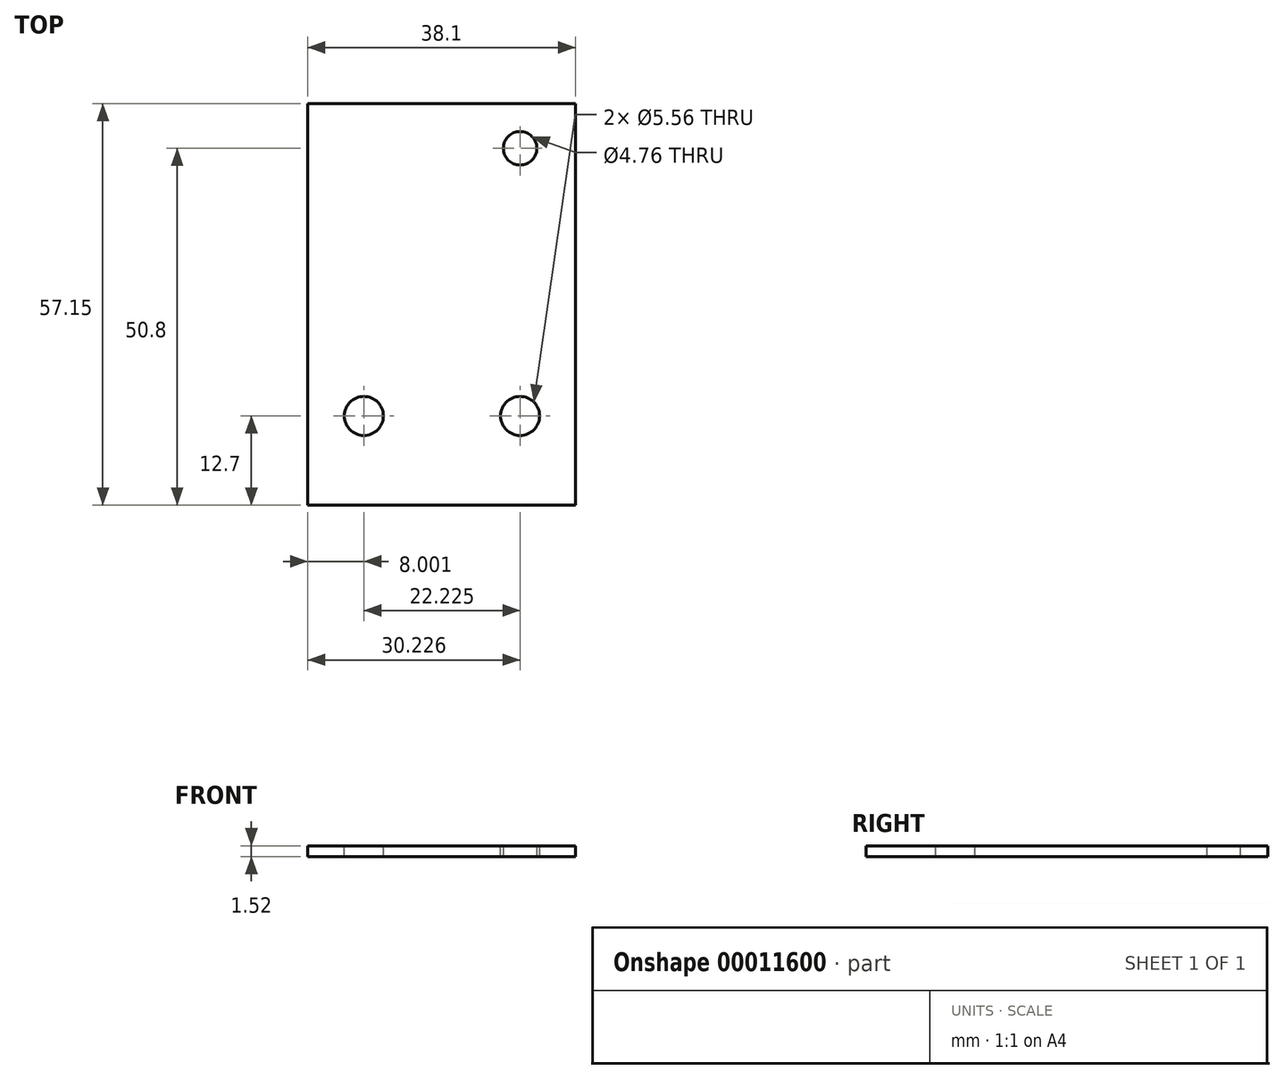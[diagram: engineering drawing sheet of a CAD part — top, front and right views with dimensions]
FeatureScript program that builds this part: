
annotation { "Feature Type Name" : "Feature", "Feature Type Description" : "" }
export const myFeature = defineFeature(function(context is Context, id is Id, definition is map)
    precondition{}
    {
        {
            var Q0;
            Q0=qCreatedBy(makeId("Top.planeOp"),FACE);
            var sketch = newSketch(context, id + "F0", { "sketchPlane" : qUnion([Q0])});
            skLineSegment(sketch, "E0.bottom", {"start": v(0, 0) * mm, "end": v(-38.1, 0) * mm});
            skLineSegment(sketch, "E0.top", {"start": v(0, -57.15) * mm, "end": v(-38.1, -57.15) * mm});
            skLineSegment(sketch, "E0.left", {"start": v(0, 0) * mm, "end": v(0, -57.15) * mm});
            skLineSegment(sketch, "E0.right", {"start": v(-38.1, 0) * mm, "end": v(-38.1, -57.15) * mm});
            skSolve(sketch);
        }
        {
            var Q0;
            Q0 = qSketchRegion(id + "F0", true);
            extrude(context, id + "F1", {"entities" : qUnion([Q0]), "depth" : 1.52 * mm});
        }
        {
            var Q0;
            Q0=qCreatedBy(makeId("Top.planeOp"),FACE);
            var sketch = newSketch(context, id + "F2", { "sketchPlane" : qUnion([Q0])});
            skPoint(sketch, "E1", {"position": v(-7.87, -6.35) * mm});
            skSolve(sketch);
        }
        {
            var Q0;
            Q0=makeQuery(id+"F1.opExtrude","CAP_FACE",FACE,{"disambiguationData":[OSD([sQuery(id+"F0.wireOp",EDGE,"E0.bottom"),sQuery(id+"F0.wireOp",EDGE,"E0.top"),sQuery(id+"F0.wireOp",EDGE,"E0.left"),sQuery(id+"F0.wireOp",EDGE,"E0.right")])],"isStart":false});
            var sketch = newSketch(context, id + "F3", { "sketchPlane" : qUnion([Q0])});
            skPoint(sketch, "E2", {"position": v(-7.87, -44.45) * mm});
            skPoint(sketch, "E3", {"position": v(-30.1, -44.45) * mm});
            skSolve(sketch);
        }
        {
            var Q0;
            Q0=sQuery(id+"F2.wireOp",VERTEX,"E1");
            var Q1;
            Q1=makeQuery(id+"F1.opExtrude","SWEPT_BODY",BODY,{"disambiguationData":[OSD([sQuery(id+"F0.wireOp",EDGE,"E0.bottom"),sQuery(id+"F0.wireOp",EDGE,"E0.top"),sQuery(id+"F0.wireOp",EDGE,"E0.left"),sQuery(id+"F0.wireOp",EDGE,"E0.right")])]});
            hole(context, id + "F4", {"style" : HoleStyle.SIMPLE, "endStyle" : HoleEndStyle.THROUGH, "oppositeDirection" : true, "holeDiameter" : 4.76 * mm, "locations" : qUnion([Q0]), "scope" : qUnion([Q1]), "isTappedThrough" : true});
        }
        {
            var Q0;
            Q0=sQuery(id+"F3.wireOp",VERTEX,"E2");
            var Q1;
            Q1=sQuery(id+"F3.wireOp",VERTEX,"E3");
            var Q2;
            Q2=makeQuery(id+"F1.opExtrude","SWEPT_BODY",BODY,{"disambiguationData":[OSD([sQuery(id+"F0.wireOp",EDGE,"E0.bottom"),sQuery(id+"F0.wireOp",EDGE,"E0.top"),sQuery(id+"F0.wireOp",EDGE,"E0.left"),sQuery(id+"F0.wireOp",EDGE,"E0.right")])]});
            hole(context, id + "F5", {"style" : HoleStyle.SIMPLE, "endStyle" : HoleEndStyle.THROUGH, "holeDiameter" : 5.56 * mm, "locations" : qUnion([Q0, Q1]), "scope" : qUnion([Q2]), "isTappedThrough" : true});
        }
    });
